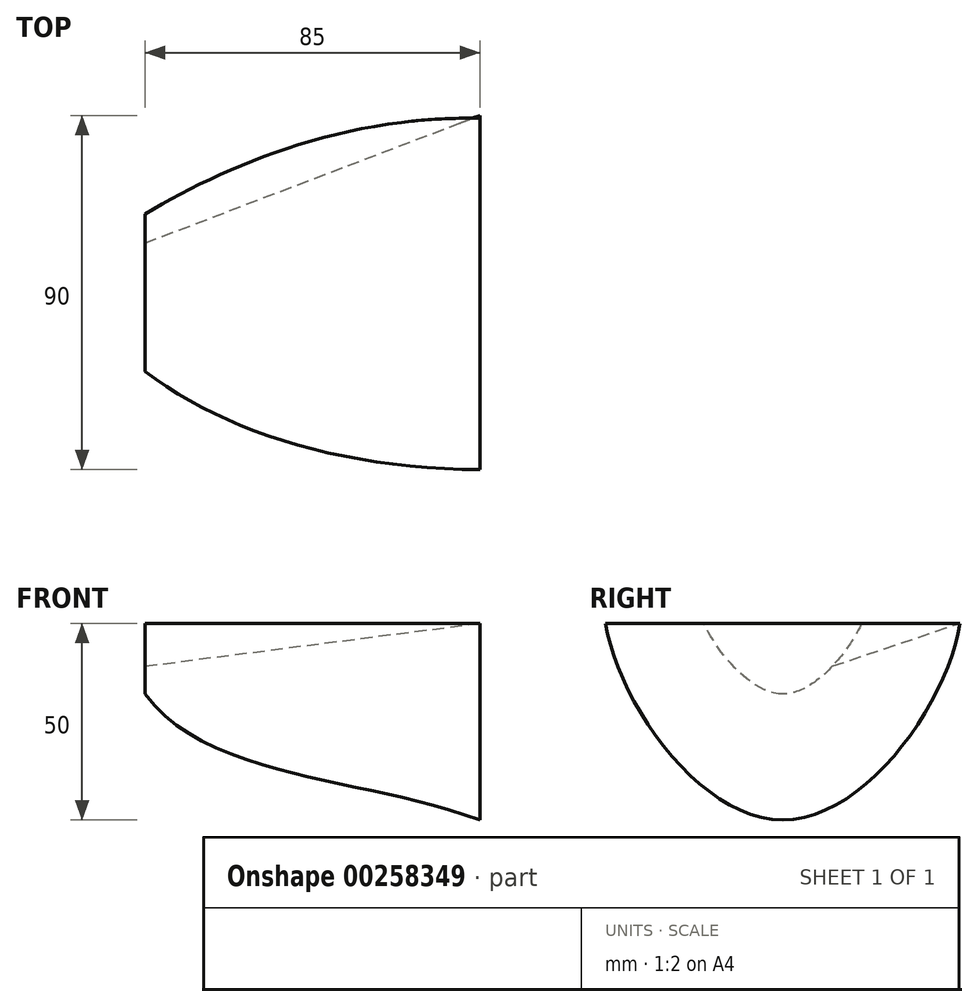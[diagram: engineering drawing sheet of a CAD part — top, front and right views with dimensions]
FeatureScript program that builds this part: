
annotation { "Feature Type Name" : "Feature", "Feature Type Description" : "" }
export const myFeature = defineFeature(function(context is Context, id is Id, definition is map)
    precondition{}
    {
        {
            var Q0;
            Q0=qCreatedBy(makeId("Right.planeOp"),FACE);
            var Q1;
            Q1 = qBodyType(qCreatedBy(id + "F1" ,EDGE), BodyType.WIRE);
            cPlane(context, id + "F0", {"entities" : qUnion([Q0, Q1]), "cplaneType" : CPlaneType.OFFSET, "offset" : 85 * mm, "oppositeDirection" : true, "width" : 150 * mm, "height" : 150 * mm});
        }
        {
            var Q0;
            Q0=qCreatedBy(makeId("Right.planeOp"),FACE);
            var sketch = newSketch(context, id + "F1", { "sketchPlane" : qUnion([Q0])});
            skFitSpline(sketch, "E0", {"points": [v(-45, 0) * mm, v(0, -50) * mm, v(45, 0) * mm], "startDerivative": vector(18, -120) * mm, "endDerivative": vector(18, 120) * mm});
            skPoint(sketch, "E1", {"position": v(0, 0) * mm});
            skLineSegment(sketch, "E2", {"start": v(-45, 0) * mm, "end": v(45, 0) * mm});
            skSolve(sketch);
        }
        {
            var Q0;
            Q0=qCreatedBy(id+"F0.planeOp",FACE);
            var sketch = newSketch(context, id + "F2", { "sketchPlane" : qUnion([Q0])});
            skFitSpline(sketch, "E3", {"points": [v(20, 0) * mm, v(0, -18) * mm, v(-20, 0) * mm], "startDerivative": vector(-12, -30) * mm, "endDerivative": vector(-12, 30) * mm});
            skLineSegment(sketch, "E4", {"start": v(-20, 0) * mm, "end": v(20, 0) * mm});
            skPoint(sketch, "E5.2", {"position": v(-45, 0) * mm});
            skPoint(sketch, "E5.3", {"position": v(45, 0) * mm});
            skSolve(sketch);
        }
        {
            var Q0;
            Q0=qCreatedBy(makeId("Top.planeOp"),FACE);
            var sketch = newSketch(context, id + "F3", { "sketchPlane" : qUnion([Q0])});
            skLineSegment(sketch, "E6.0", {"start": v(-85, -20) * mm, "end": v(-85, 20) * mm});
            skFitSpline(sketch, "E7", {"points": [v(-85, 20) * mm, v(0, 44.27) * mm], "startDerivative": vector(60, 36) * mm, "endDerivative": vector(105, -2.19) * mm});
            skSolve(sketch);
        }
        {
            var Q0;
            Q0=qCreatedBy(makeId("Top.planeOp"),FACE);
            var sketch = newSketch(context, id + "F4", { "sketchPlane" : qUnion([Q0])});
            skPoint(sketch, "E8.0", {"position": v(-85, -20) * mm});
            skPoint(sketch, "E9.0", {"position": v(0, -45) * mm});
            skFitSpline(sketch, "E10", {"points": [v(-85, -20) * mm, v(0, -45) * mm], "startDerivative": vector(60, -46.29) * mm, "endDerivative": vector(105, -0.9) * mm});
            skSolve(sketch);
        }
        {
            var Q0;
            Q0=qCreatedBy(makeId("Front.planeOp"),FACE);
            var sketch = newSketch(context, id + "F5", { "sketchPlane" : qUnion([Q0])});
            skPoint(sketch, "E11.0", {"position": v(-85, -18) * mm});
            skPoint(sketch, "E12.0", {"position": v(0, -50) * mm});
            skFitSpline(sketch, "E13", {"points": [v(-85, -18) * mm, v(0, -50) * mm], "startDerivative": vector(45, -64.22) * mm, "endDerivative": vector(85, -32) * mm});
            skPoint(sketch, "E14.0", {"position": v(0, 0) * mm});
            skSolve(sketch);
        }
        {
            var Q0;
            Q0=makeQuery(id+"F2.imprint","IMPRINT",FACE,{"disambiguationData":[TD([[makeQuery(id+"F2.imprint","IMPRINT",EDGE,{"derivedFrom":sQuery(id+"F2.wireOp",EDGE,"E3")}),-1.0]])]});
            var Q1;
            Q1=makeQuery(id+"F1.imprint","IMPRINT",FACE,{"disambiguationData":[TD([[makeQuery(id+"F1.imprint","IMPRINT",EDGE,{"derivedFrom":sQuery(id+"F1.wireOp",EDGE,"E0")}),1.0]])]});
            var Q2;
            Q2=sQuery(id+"F5.wireOp",EDGE,"E13");
            var Q3;
            Q3=sQuery(id+"F3.wireOp",EDGE,"E7");
            var Q4;
            Q4=sQuery(id+"F4.wireOp",EDGE,"E10");
            loft(context, id + "F6", {"addGuides" : true, "sheetProfilesArray" : [{ "sheetProfileEntities" : qUnion([Q0]) }, { "sheetProfileEntities" : qUnion([Q1]) }], "guidesArray" : [{ "guideEntities" : qUnion([Q2]), "guideDerivativeType" : LoftGuideDerivativeType.DEFAULT, "guideDerivativeMagnitude" : 1 }, { "guideEntities" : qUnion([Q3]), "guideDerivativeType" : LoftGuideDerivativeType.DEFAULT, "guideDerivativeMagnitude" : 1 }, { "guideEntities" : qUnion([Q4]), "guideDerivativeType" : LoftGuideDerivativeType.DEFAULT, "guideDerivativeMagnitude" : 1 }]});
        }
    });
